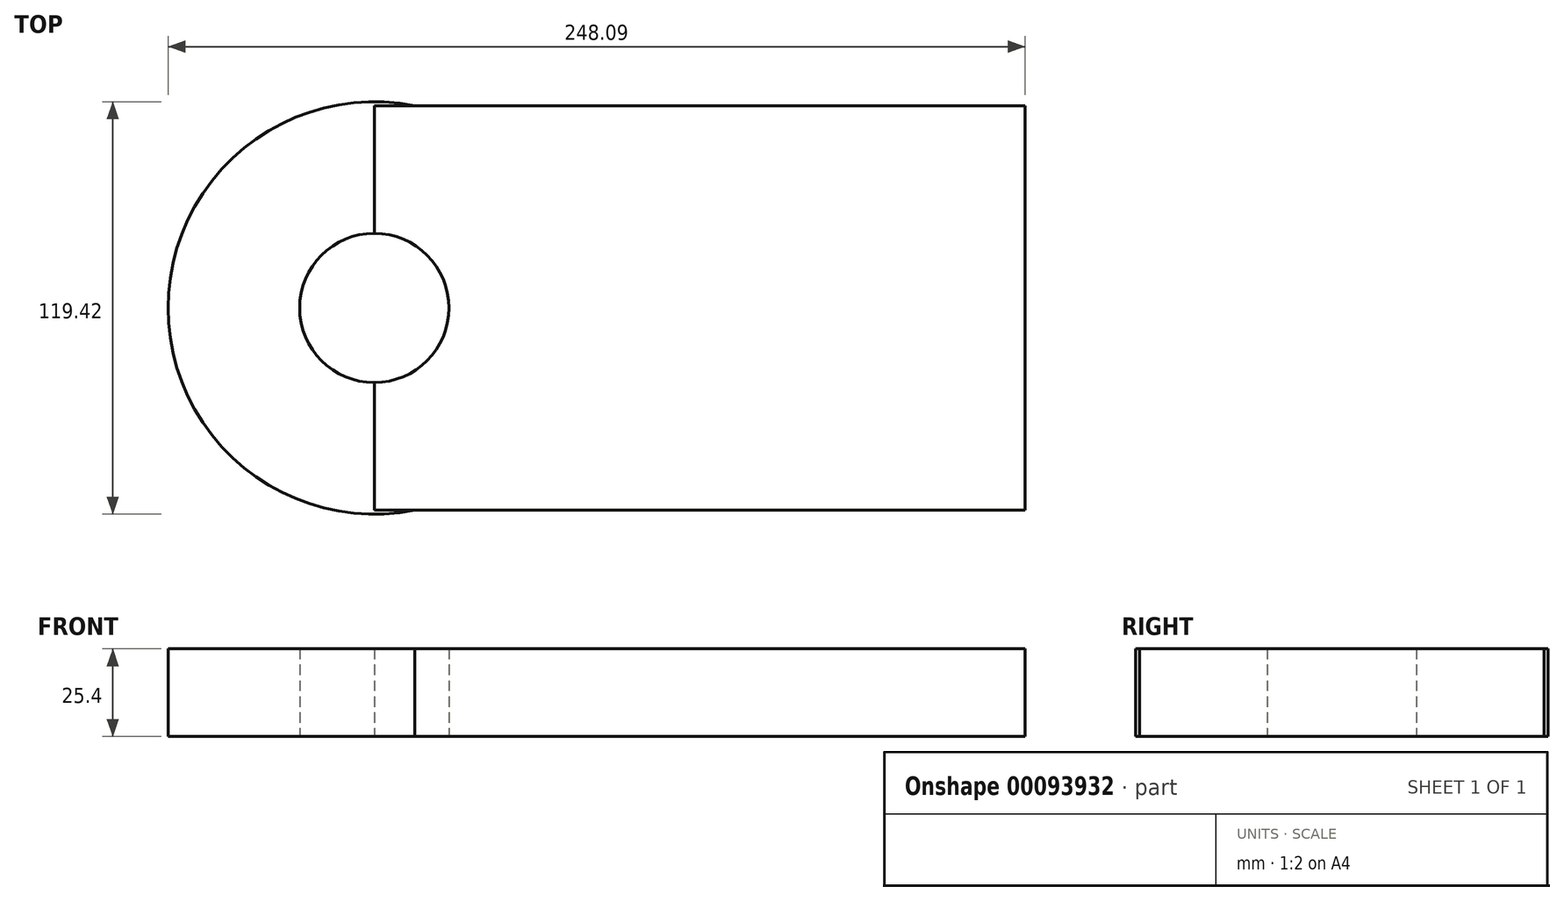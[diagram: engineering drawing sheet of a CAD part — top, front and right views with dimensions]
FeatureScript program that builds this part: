
annotation { "Feature Type Name" : "Feature", "Feature Type Description" : "" }
export const myFeature = defineFeature(function(context is Context, id is Id, definition is map)
    precondition{}
    {
        {
            var Q0;
            Q0=qCreatedBy(makeId("Top.planeOp"),FACE);
            var sketch = newSketch(context, id + "F0", { "sketchPlane" : qUnion([Q0])});
            skLineSegment(sketch, "E0.bottom", {"start": v(-94.19, 58.55) * mm, "end": v(94.19, 58.55) * mm});
            skLineSegment(sketch, "E0.top", {"start": v(-94.19, -58.55) * mm, "end": v(94.19, -58.55) * mm});
            skLineSegment(sketch, "E0.left", {"start": v(-94.19, 58.55) * mm, "end": v(-94.19, -58.55) * mm});
            skLineSegment(sketch, "E0.right", {"start": v(94.19, 58.55) * mm, "end": v(94.19, -58.55) * mm});
            skPoint(sketch, "E0.middle", {"position": v(0, 0) * mm});
            skCircle(sketch, "E1", {"center": v(-94.19, 0) * mm, "radius": 21.61 * mm});
            skCircle(sketch, "E2", {"center": v(-94.19, 0) * mm, "radius": 59.7 * mm});
            skSolve(sketch);
        }
        {
            var Q0;
            Q0=qCreatedBy(makeId("Top.planeOp"),FACE);
            var sketch = newSketch(context, id + "F1", { "sketchPlane" : qUnion([Q0])});
            skSolve(sketch);
        }
        {
            var Q0;
            {var subQ0=sQuery(id+"F0.wireOp",EDGE,"E0.left");var subQ5=sQuery(id+"F0.wireOp",EDGE,"E0.bottom");var subQ6=makeQuery(id+"F0.imprint","INTERSECT",VERTEX,{"derivedFrom":[subQ5,subQ0]});Q0=makeQuery(id+"F0.imprint","IMPRINT",FACE,{"disambiguationData":[TD([[makeQuery(id+"F0.imprint","IMPRINT",EDGE,{"disambiguationData":[TD([[subQ6,-1.0]])],"derivedFrom":subQ5}),1.0]])]});}
            var sketch = newSketch(context, id + "F2", { "sketchPlane" : qUnion([Q0])});
            skSolve(sketch);
        }
        {
            var Q0;
            {var subQ0=sQuery(id+"F0.wireOp",EDGE,"E0.right");Q0=makeQuery(id+"F0.imprint","IMPRINT",FACE,{"disambiguationData":[TD([[makeQuery(id+"F0.imprint","IMPRINT",EDGE,{"derivedFrom":subQ0}),-1.0]])]});}
            var Q1;
            {var subQ0=sQuery(id+"F0.wireOp",EDGE,"E0.left");var subQ5=sQuery(id+"F0.wireOp",EDGE,"E0.bottom");var subQ6=makeQuery(id+"F0.imprint","INTERSECT",VERTEX,{"derivedFrom":[subQ5,subQ0]});Q1=makeQuery(id+"F2.imprint","IMPRINT",FACE,{"disambiguationData":[TD([[makeQuery(id+"F2.imprint","IMPRINT",EDGE,{"derivedFrom":makeQuery(id+"F0.imprint","IMPRINT",EDGE,{"disambiguationData":[TD([[subQ6,-1.0]])],"derivedFrom":subQ5})}),1.0]])]});}
            var Q2;
            {var subQ0=sQuery(id+"F0.wireOp",EDGE,"E0.left");var subQ5=sQuery(id+"F0.wireOp",EDGE,"E0.bottom");var subQ6=makeQuery(id+"F0.imprint","INTERSECT",VERTEX,{"derivedFrom":[subQ5,subQ0]});Q2=makeQuery(id+"F0.imprint","IMPRINT",FACE,{"disambiguationData":[TD([[makeQuery(id+"F0.imprint","IMPRINT",EDGE,{"disambiguationData":[TD([[subQ6,-1.0]])],"derivedFrom":subQ5}),-1.0]])]});}
            extrude(context, id + "F3", {"entities" : qUnion([Q0, Q1, Q2]), "depth" : 25.4 * mm});
        }
    });
